# Revit family: Shower-Showerhead-KOHLER-Purist-K-14486BR
name_source: partatom
category: Plumbing Fixtures
revit_build: Autodesk Revit 2017 (Build: 20160225_1515(x64)
units: mm (PartAtom-declared; Revit-internal decimal feet)

## family parameters
Cut with Voids When Loaded = No
Host = Face
OmniClass Number = 23.31.17.00
OmniClass Title = Showers
Part Type = Normal
Room Calculation Point = No
Round Connector Dimension = Use Diameter
Shared = No

## types (2) — shared parameters
ADA Compliant = No
Assembly Code = D2010700
CW Connection = No
Cold Water Inlet = Cold Water Inlet
Date Modified = 09/16/2020
Default Elevation = 0"
Description = SINGLE-FUNCTION KATALST SHOWRHEAD
Drain Included = No
Flow Rate = 0 GPM
HW Connection = Yes
Height = 3 11/16"
Hot Water Inlet = Tempared Water Inlet
Length = 5 1/2"
Manufacturer = KOHLER Co.
Master Format 2014 = 22 42 23
Master Format 2014 Name = Residential Showers
Material = Premium Metal Construction
Pressure = 0.00 psi
Product Name = Purist
Product Page URL = https://br.kohler.com
URL = https://br.kohler.com
Vent Connection = No
Waste Connection = No
Waste Water Outlet = Waste Water Outlet
WaterSense Certified = No
Width = 5 1/2"

## per-type parameters (varying)
| type | Finish | Model | Type |
| CP-Polished Chrome | Kohler-Metal-CP-Polished_Chrome | K-14486BR-AK-CP | 1 |
| BN-Brushed Nickel | Kohler-Metal-BN-Vibrant_Brushed_Nickel | K-14486BR-AK-BN | 2 |

## geometry (parser evidence)
native form markers: Sweep x4
no freeform markers — native parametric forms only
